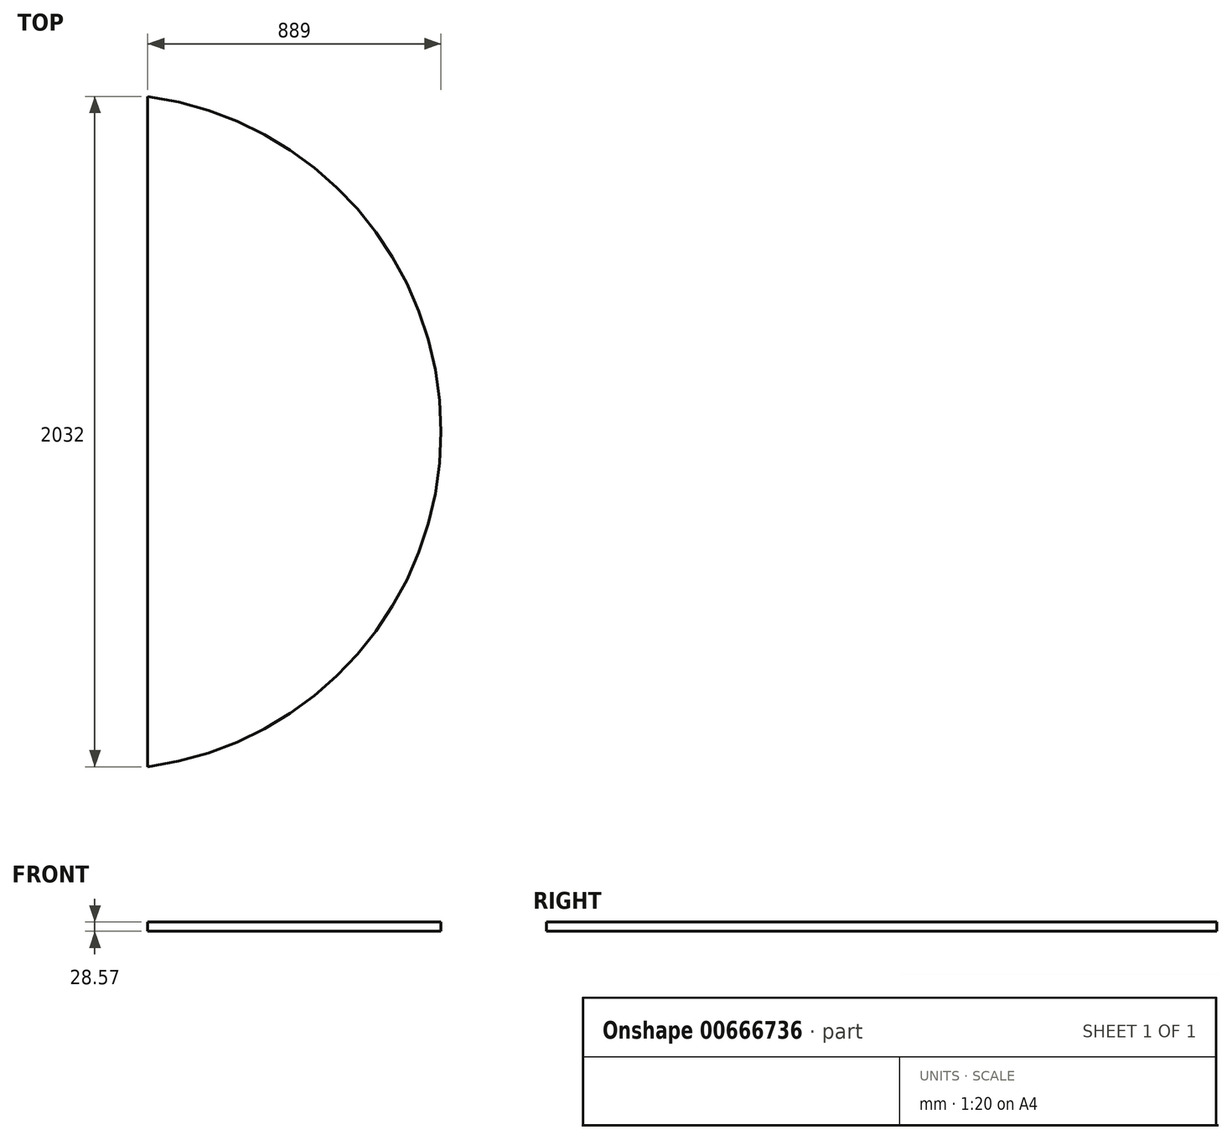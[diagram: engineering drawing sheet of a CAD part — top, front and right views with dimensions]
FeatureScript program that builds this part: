
annotation { "Feature Type Name" : "Feature", "Feature Type Description" : "" }
export const myFeature = defineFeature(function(context is Context, id is Id, definition is map)
    precondition{}
    {
        {
            var Q0;
            Q0=qCreatedBy(makeId("Top.planeOp"),FACE);
            var sketch = newSketch(context, id + "F0", { "sketchPlane" : qUnion([Q0])});
            skLineSegment(sketch, "E0.bottom", {"start": v(444.5, 1016) * mm, "end": v(-444.5, 1016) * mm});
            skLineSegment(sketch, "E0.top", {"start": v(444.5, -1016) * mm, "end": v(-444.5, -1016) * mm});
            skLineSegment(sketch, "E0.left", {"start": v(444.5, 1016) * mm, "end": v(444.5, -1016) * mm});
            skLineSegment(sketch, "E0.right", {"start": v(-444.5, 1016) * mm, "end": v(-444.5, -1016) * mm});
            skPoint(sketch, "E0.middle", {"position": v(0, 0) * mm});
            skLineSegment(sketch, "E1", {"start": v(444.5, 0) * mm, "end": v(-444.5, 0) * mm});
            skArc(sketch, "E2", {"start": v(-444.5, -1016) * mm, "mid": v(444.5, 0) * mm, "end": v(-444.5, 1016) * mm});
            skSolve(sketch);
        }
        {
            var Q0;
            {var subQ3=sQuery(id+"F0.wireOp",EDGE,"E1");Q0=makeQuery(id+"F0.imprint","IMPRINT",FACE,{"disambiguationData":[TD([[makeQuery(id+"F0.imprint","IMPRINT",EDGE,{"derivedFrom":subQ3}),-1.0]])]});}
            var Q1;
            {var subQ3=sQuery(id+"F0.wireOp",EDGE,"E1");Q1=makeQuery(id+"F0.imprint","IMPRINT",FACE,{"disambiguationData":[TD([[makeQuery(id+"F0.imprint","IMPRINT",EDGE,{"derivedFrom":subQ3}),1.0]])]});}
            extrude(context, id + "F1", {"entities" : qUnion([Q0, Q1]), "depth" : 28.57 * mm, "offsetDistance" : 25.4 * mm});
        }
    });
